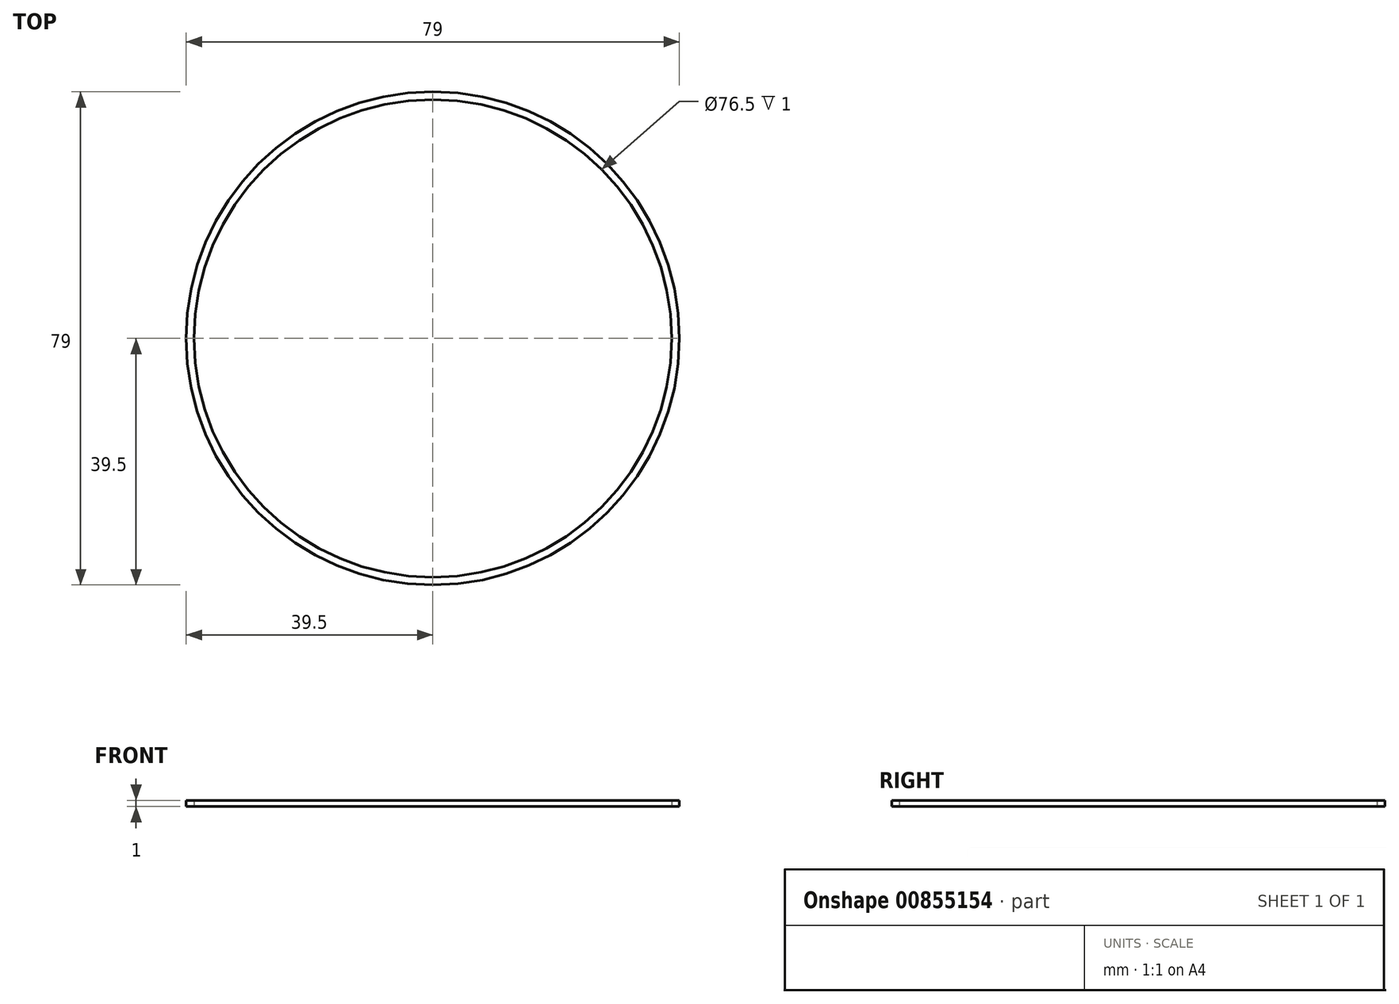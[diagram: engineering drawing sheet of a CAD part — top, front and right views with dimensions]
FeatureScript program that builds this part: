
annotation { "Feature Type Name" : "Feature", "Feature Type Description" : "" }
export const myFeature = defineFeature(function(context is Context, id is Id, definition is map)
    precondition{}
    {
        {
            var Q0;
            Q0=qCreatedBy(makeId("Top.planeOp"),FACE);
            var sketch = newSketch(context, id + "F0", { "sketchPlane" : qUnion([Q0])});
            skCircle(sketch, "E0", {"center": v(0, 0) * mm, "radius": 39.5 * mm});
            skCircle(sketch, "E1", {"center": v(0, 0) * mm, "radius": 38.25 * mm});
            skSolve(sketch);
        }
        {
            var Q0;
            Q0 = qSketchRegion(id + "F0", true);
            extrude(context, id + "F1", {"entities" : qUnion([Q0]), "depth" : 1 * mm, "offsetDistance" : 25 * mm});
        }
    });
